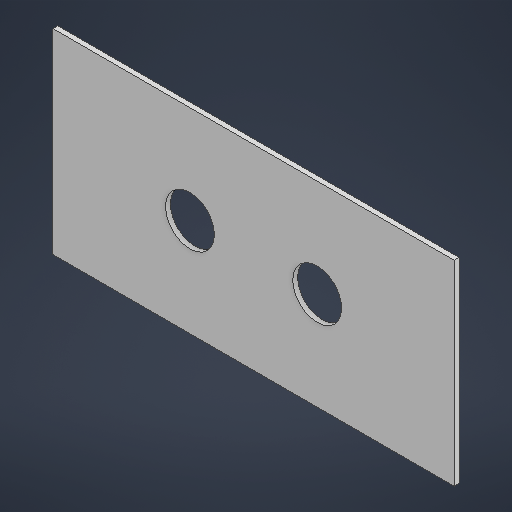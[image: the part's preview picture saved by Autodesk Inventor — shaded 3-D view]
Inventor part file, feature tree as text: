
AUTODESK INVENTOR PART (.ipt)
format: ipt  version: 2025 (Build 290162000, 162)  size: 177,152 bytes
history: native  units: in
note: dims shown in document units (in); Inventor stores cm internally (conversion verified against a paired STEP export)
features: extrude x1, sketch x1
ambient origin geometry x8: Origin, YZ Plane, XZ Plane, XY Plane, X Axis, Y Axis, Z Axis, Center Point
bodies: Solid1 (feature_tree)
feature tree (2):
  extrude  "Extrusion1"  Depth=0.7874in
  sketch  "Sketch1"  dims[d0=1.6142in d1=0.7874in d2=0.1969in d3=0.2559in d4=0.1969in d5=0.2559in d6=0.0197in d7=0.0in]
